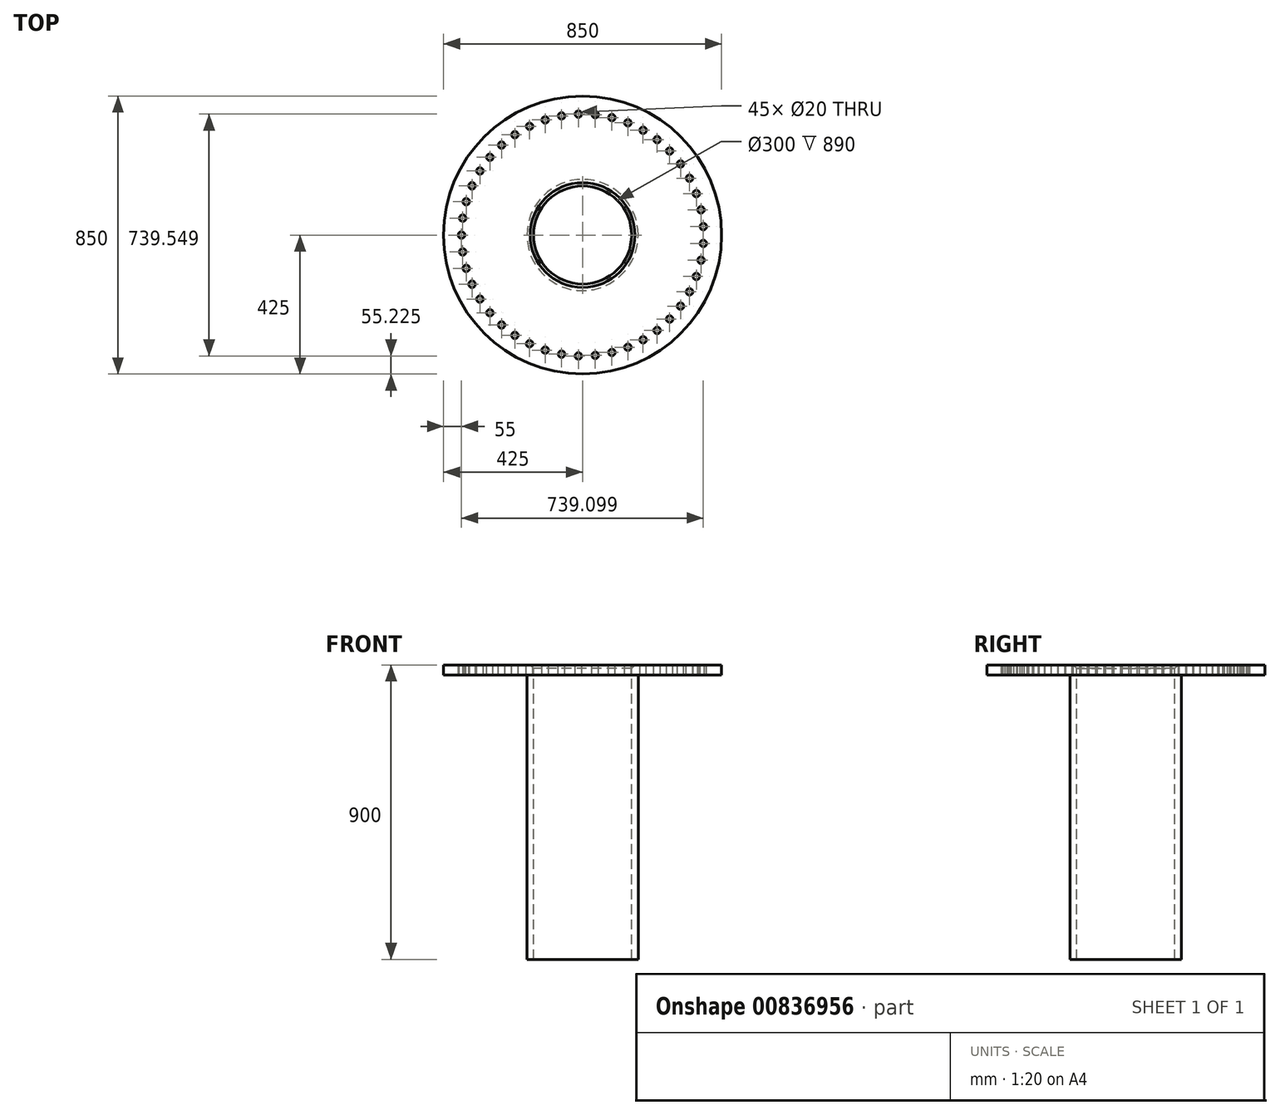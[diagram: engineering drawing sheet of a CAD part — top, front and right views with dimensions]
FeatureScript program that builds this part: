
annotation { "Feature Type Name" : "Feature", "Feature Type Description" : "" }
export const myFeature = defineFeature(function(context is Context, id is Id, definition is map)
    precondition{}
    {
        {
            var Q0;
            Q0=qCreatedBy(makeId("Top.planeOp"),FACE);
            var sketch = newSketch(context, id + "F0", { "sketchPlane" : qUnion([Q0])});
            skLineSegment(sketch, "E0.bottom", {"start": v(-1185, 450) * mm, "end": v(1185, 450) * mm});
            skLineSegment(sketch, "E0.top", {"start": v(-1185, -450) * mm, "end": v(1185, -450) * mm});
            skLineSegment(sketch, "E0.left", {"start": v(-1185, 450) * mm, "end": v(-1185, -450) * mm});
            skLineSegment(sketch, "E0.right", {"start": v(1185, 450) * mm, "end": v(1185, -450) * mm});
            skPoint(sketch, "E0.middle", {"position": v(0, 0) * mm});
            skLineSegment(sketch, "E1.bottom", {"start": v(-1185, 450) * mm, "end": v(-1141.5, 450) * mm});
            skLineSegment(sketch, "E1.top", {"start": v(-1185, -450) * mm, "end": v(-1141.5, -450) * mm});
            skLineSegment(sketch, "E1.right", {"start": v(-1141.49, 450) * mm, "end": v(-1141.49, -450) * mm});
            skLineSegment(sketch, "E2", {"start": v(1185, 0) * mm, "end": v(-1185, 0) * mm, "construction": true});
            skLineSegment(sketch, "E3", {"start": v(-92.5, -600) * mm, "end": v(-92.5, 600) * mm, "construction": true});
            skCircle(sketch, "E4", {"center": v(-92.5, 0) * mm, "radius": 600 * mm});
            skCircle(sketch, "E5", {"center": v(-92.5, 0) * mm, "radius": 550 * mm});
            skCircle(sketch, "E6", {"center": v(-92.5, 0) * mm, "radius": 425 * mm});
            skCircle(sketch, "E7", {"center": v(-92.5, 0) * mm, "radius": 525 * mm});
            skCircle(sketch, "E8", {"center": v(-617.5, 0) * mm, "radius": 10 * mm});
            skCircle(sketch, "E9.1.0", {"center": v(-612.4, -73.07) * mm, "radius": 10 * mm});
            skCircle(sketch, "E9.2.0", {"center": v(-597.16, -144.7) * mm, "radius": 10 * mm});
            skCircle(sketch, "E10.1.3.0", {"center": v(-572.11, -213.54) * mm, "radius": 10 * mm});
            skCircle(sketch, "E10.1.4.0", {"center": v(-537.73, -278.2) * mm, "radius": 10 * mm});
            skCircle(sketch, "E10.1.5.0", {"center": v(-494.67, -337.46) * mm, "radius": 10 * mm});
            skCircle(sketch, "E10.1.6.0", {"center": v(-443.8, -390.15) * mm, "radius": 10 * mm});
            skCircle(sketch, "E10.1.7.0", {"center": v(-386.08, -435.24) * mm, "radius": 10 * mm});
            skCircle(sketch, "E10.1.8.0", {"center": v(-322.64, -471.87) * mm, "radius": 10 * mm});
            skCircle(sketch, "E10.1.9.0", {"center": v(-254.73, -499.3) * mm, "radius": 10 * mm});
            skCircle(sketch, "E10.1.10.0", {"center": v(-183.67, -517.02) * mm, "radius": 10 * mm});
            skCircle(sketch, "E10.1.11.0", {"center": v(-110.82, -524.68) * mm, "radius": 10 * mm});
            skCircle(sketch, "E10.1.12.0", {"center": v(-37.62, -522.12) * mm, "radius": 10 * mm});
            skCircle(sketch, "E10.1.13.0", {"center": v(34.5, -509.4) * mm, "radius": 10 * mm});
            skCircle(sketch, "E10.1.14.0", {"center": v(104.17, -486.77) * mm, "radius": 10 * mm});
            skCircle(sketch, "E10.1.15.0", {"center": v(170, -454.66) * mm, "radius": 10 * mm});
            skCircle(sketch, "E10.1.16.0", {"center": v(230.72, -413.7) * mm, "radius": 10 * mm});
            skCircle(sketch, "E10.1.17.0", {"center": v(285.15, -364.7) * mm, "radius": 10 * mm});
            skCircle(sketch, "E10.1.18.0", {"center": v(332.23, -308.59) * mm, "radius": 10 * mm});
            skCircle(sketch, "E10.1.19.0", {"center": v(371.05, -246.47) * mm, "radius": 10 * mm});
            skCircle(sketch, "E10.1.20.0", {"center": v(400.84, -179.56) * mm, "radius": 10 * mm});
            skCircle(sketch, "E10.1.21.0", {"center": v(421.03, -109.15) * mm, "radius": 10 * mm});
            skCircle(sketch, "E10.1.22.0", {"center": v(431.22, -36.62) * mm, "radius": 10 * mm});
            skCircle(sketch, "E10.1.23.0", {"center": v(431.22, 36.62) * mm, "radius": 10 * mm});
            skCircle(sketch, "E10.1.24.0", {"center": v(421.03, 109.15) * mm, "radius": 10 * mm});
            skCircle(sketch, "E10.1.25.0", {"center": v(400.84, 179.56) * mm, "radius": 10 * mm});
            skCircle(sketch, "E10.1.26.0", {"center": v(371.05, 246.47) * mm, "radius": 10 * mm});
            skCircle(sketch, "E10.1.27.0", {"center": v(332.23, 308.59) * mm, "radius": 10 * mm});
            skCircle(sketch, "E10.1.28.0", {"center": v(285.15, 364.7) * mm, "radius": 10 * mm});
            skCircle(sketch, "E10.1.29.0", {"center": v(230.72, 413.7) * mm, "radius": 10 * mm});
            skCircle(sketch, "E10.1.30.0", {"center": v(170, 454.66) * mm, "radius": 10 * mm});
            skCircle(sketch, "E10.1.31.0", {"center": v(104.17, 486.77) * mm, "radius": 10 * mm});
            skCircle(sketch, "E10.1.32.0", {"center": v(34.5, 509.4) * mm, "radius": 10 * mm});
            skCircle(sketch, "E10.1.33.0", {"center": v(-37.62, 522.12) * mm, "radius": 10 * mm});
            skCircle(sketch, "E10.1.34.0", {"center": v(-110.82, 524.68) * mm, "radius": 10 * mm});
            skCircle(sketch, "E10.1.35.0", {"center": v(-183.67, 517.02) * mm, "radius": 10 * mm});
            skCircle(sketch, "E10.1.36.0", {"center": v(-254.73, 499.3) * mm, "radius": 10 * mm});
            skCircle(sketch, "E10.1.37.0", {"center": v(-322.64, 471.87) * mm, "radius": 10 * mm});
            skCircle(sketch, "E10.1.38.0", {"center": v(-386.08, 435.24) * mm, "radius": 10 * mm});
            skCircle(sketch, "E10.1.39.0", {"center": v(-443.8, 390.15) * mm, "radius": 10 * mm});
            skCircle(sketch, "E10.1.40.0", {"center": v(-494.67, 337.46) * mm, "radius": 10 * mm});
            skCircle(sketch, "E10.1.41.0", {"center": v(-537.73, 278.2) * mm, "radius": 10 * mm});
            skCircle(sketch, "E10.1.42.0", {"center": v(-572.11, 213.54) * mm, "radius": 10 * mm});
            skCircle(sketch, "E10.1.43.0", {"center": v(-597.16, 144.7) * mm, "radius": 10 * mm});
            skCircle(sketch, "E10.1.44.0", {"center": v(-612.4, 73.07) * mm, "radius": 10 * mm});
            skCircle(sketch, "E11", {"center": v(-92.5, 0) * mm, "radius": 370 * mm});
            skCircle(sketch, "E12", {"center": v(-462.5, 0) * mm, "radius": 10 * mm});
            skCircle(sketch, "E13.1.0", {"center": v(-458.9, -51.5) * mm, "radius": 10 * mm});
            skCircle(sketch, "E13.2.0", {"center": v(-448.17, -101.99) * mm, "radius": 10 * mm});
            skCircle(sketch, "E13.3.0", {"center": v(-430.51, -150.5) * mm, "radius": 10 * mm});
            skCircle(sketch, "E13.4.0", {"center": v(-406.28, -196.07) * mm, "radius": 10 * mm});
            skCircle(sketch, "E13.5.0", {"center": v(-375.94, -237.83) * mm, "radius": 10 * mm});
            skCircle(sketch, "E13.6.0", {"center": v(-340.08, -274.96) * mm, "radius": 10 * mm});
            skCircle(sketch, "E13.7.0", {"center": v(-299.4, -306.74) * mm, "radius": 10 * mm});
            skCircle(sketch, "E13.8.0", {"center": v(-254.7, -332.55) * mm, "radius": 10 * mm});
            skCircle(sketch, "E13.9.0", {"center": v(-206.84, -351.9) * mm, "radius": 10 * mm});
            skCircle(sketch, "E13.10.0", {"center": v(-156.75, -364.38) * mm, "radius": 10 * mm});
            skCircle(sketch, "E13.11.0", {"center": v(-105.41, -369.77) * mm, "radius": 10 * mm});
            skCircle(sketch, "E13.12.0", {"center": v(-53.82, -367.97) * mm, "radius": 10 * mm});
            skCircle(sketch, "E13.13.0", {"center": v(-2.99, -359) * mm, "radius": 10 * mm});
            skCircle(sketch, "E13.14.0", {"center": v(46.1, -343.06) * mm, "radius": 10 * mm});
            skCircle(sketch, "E13.15.0", {"center": v(92.5, -320.43) * mm, "radius": 10 * mm});
            skCircle(sketch, "E13.16.0", {"center": v(135.3, -291.56) * mm, "radius": 10 * mm});
            skCircle(sketch, "E13.17.0", {"center": v(173.66, -257.02) * mm, "radius": 10 * mm});
            skCircle(sketch, "E13.18.0", {"center": v(206.84, -217.48) * mm, "radius": 10 * mm});
            skCircle(sketch, "E13.19.0", {"center": v(234.2, -173.7) * mm, "radius": 10 * mm});
            skCircle(sketch, "E13.20.0", {"center": v(255.19, -126.55) * mm, "radius": 10 * mm});
            skCircle(sketch, "E13.21.0", {"center": v(269.41, -76.93) * mm, "radius": 10 * mm});
            skCircle(sketch, "E13.22.0", {"center": v(276.6, -25.8) * mm, "radius": 10 * mm});
            skCircle(sketch, "E13.23.0", {"center": v(276.6, 25.8) * mm, "radius": 10 * mm});
            skCircle(sketch, "E13.24.0", {"center": v(269.41, 76.93) * mm, "radius": 10 * mm});
            skCircle(sketch, "E13.25.0", {"center": v(255.19, 126.55) * mm, "radius": 10 * mm});
            skCircle(sketch, "E13.26.0", {"center": v(234.2, 173.7) * mm, "radius": 10 * mm});
            skCircle(sketch, "E13.27.0", {"center": v(206.84, 217.48) * mm, "radius": 10 * mm});
            skCircle(sketch, "E13.28.0", {"center": v(173.66, 257.02) * mm, "radius": 10 * mm});
            skCircle(sketch, "E13.29.0", {"center": v(135.3, 291.56) * mm, "radius": 10 * mm});
            skCircle(sketch, "E13.30.0", {"center": v(92.5, 320.43) * mm, "radius": 10 * mm});
            skCircle(sketch, "E13.31.0", {"center": v(46.1, 343.06) * mm, "radius": 10 * mm});
            skCircle(sketch, "E13.32.0", {"center": v(-2.99, 359) * mm, "radius": 10 * mm});
            skCircle(sketch, "E13.33.0", {"center": v(-53.82, 367.97) * mm, "radius": 10 * mm});
            skCircle(sketch, "E13.34.0", {"center": v(-105.41, 369.77) * mm, "radius": 10 * mm});
            skCircle(sketch, "E13.35.0", {"center": v(-156.75, 364.38) * mm, "radius": 10 * mm});
            skCircle(sketch, "E13.36.0", {"center": v(-206.84, 351.9) * mm, "radius": 10 * mm});
            skCircle(sketch, "E13.37.0", {"center": v(-254.7, 332.55) * mm, "radius": 10 * mm});
            skCircle(sketch, "E13.38.0", {"center": v(-299.4, 306.74) * mm, "radius": 10 * mm});
            skCircle(sketch, "E13.39.0", {"center": v(-340.08, 274.96) * mm, "radius": 10 * mm});
            skCircle(sketch, "E13.40.0", {"center": v(-375.94, 237.83) * mm, "radius": 10 * mm});
            skCircle(sketch, "E13.41.0", {"center": v(-406.28, 196.07) * mm, "radius": 10 * mm});
            skCircle(sketch, "E13.42.0", {"center": v(-430.51, 150.5) * mm, "radius": 10 * mm});
            skCircle(sketch, "E13.43.0", {"center": v(-448.17, 101.99) * mm, "radius": 10 * mm});
            skCircle(sketch, "E13.44.0", {"center": v(-458.9, 51.5) * mm, "radius": 10 * mm});
            skLineSegment(sketch, "E14.bottom", {"start": v(-925, 450) * mm, "end": v(-735, 450) * mm});
            skLineSegment(sketch, "E14.top", {"start": v(-925, 315) * mm, "end": v(-735, 315) * mm});
            skLineSegment(sketch, "E14.left", {"start": v(-925, 450) * mm, "end": v(-925, 315) * mm});
            skLineSegment(sketch, "E14.right", {"start": v(-735, 450) * mm, "end": v(-735, 315) * mm});
            skLineSegment(sketch, "E15.bottom", {"start": v(-913, 327) * mm, "end": v(-747, 327) * mm});
            skLineSegment(sketch, "E15.top", {"start": v(-913, 438) * mm, "end": v(-747, 438) * mm});
            skLineSegment(sketch, "E15.left", {"start": v(-913, 327) * mm, "end": v(-913, 438) * mm});
            skLineSegment(sketch, "E15.right", {"start": v(-747, 327) * mm, "end": v(-747, 438) * mm});
            skPoint(sketch, "E15.middle", {"position": v(-830, 382.5) * mm});
            skLineSegment(sketch, "E16.MirrorCS", {"start": v(-735, -450) * mm, "end": v(-735, -315) * mm});
            skLineSegment(sketch, "E17.MirrorCS", {"start": v(-925, -315) * mm, "end": v(-735, -315) * mm});
            skLineSegment(sketch, "E18.MirrorCS", {"start": v(-913, -438) * mm, "end": v(-747, -438) * mm});
            skLineSegment(sketch, "E19.MirrorCS", {"start": v(-925, -450) * mm, "end": v(-925, -315) * mm});
            skLineSegment(sketch, "E20.MirrorCS", {"start": v(-747, -327) * mm, "end": v(-747, -438) * mm});
            skPoint(sketch, "E21.MirrorP", {"position": v(-830, -382.5) * mm});
            skLineSegment(sketch, "E22.MirrorCS", {"start": v(-913, -327) * mm, "end": v(-913, -438) * mm});
            skLineSegment(sketch, "E23.MirrorCS", {"start": v(-913, -327) * mm, "end": v(-747, -327) * mm});
            skLineSegment(sketch, "E24.MirrorCS", {"start": v(-925, -450) * mm, "end": v(-735, -450) * mm});
            skArc(sketch, "E25", {"start": v(-301.83, -562.3) * mm, "mid": v(-739.86, -478.19) * mm, "end": v(-1185, -450) * mm});
            skArc(sketch, "E26.MirrorCS", {"start": v(-301.83, 562.3) * mm, "mid": v(-739.86, 478.19) * mm, "end": v(-1185, 450) * mm});
            skCircle(sketch, "E27", {"center": v(-92.5, 0) * mm, "radius": 325 * mm});
            skCircle(sketch, "E28", {"center": v(-92.5, 0) * mm, "radius": 150 * mm});
            skCircle(sketch, "E29", {"center": v(-92.5, 0) * mm, "radius": 170 * mm});
            skSolve(sketch);
        }
        {
            var Q0;
            {var subQ130=sQuery(id+"F0.wireOp",EDGE,"E6");var subQ131=makeQuery(id+"F0.imprint","INTERSECT",VERTEX,{"derivedFrom":[sQuery(id+"F0.wireOp",EDGE,"E0.bottom"),subQ130]});Q0=makeQuery(id+"F0.imprint","IMPRINT",FACE,{"disambiguationData":[TD([[makeQuery(id+"F0.imprint","IMPRINT",EDGE,{"disambiguationData":[TD([[subQ131,-1.0]])],"derivedFrom":subQ130}),1.0]])]});}
            var Q1;
            Q1=makeQuery(id+"F0.imprint","IMPRINT",FACE,{"disambiguationData":[TD([[makeQuery(id+"F0.imprint","IMPRINT",EDGE,{"derivedFrom":sQuery(id+"F0.wireOp",EDGE,"E27")}),-1.0]])]});
            var Q2;
            Q2=makeQuery(id+"F0.imprint","IMPRINT",FACE,{"disambiguationData":[TD([[makeQuery(id+"F0.imprint","IMPRINT",EDGE,{"derivedFrom":sQuery(id+"F0.wireOp",EDGE,"E27")}),1.0]])]});
            extrude(context, id + "F1", {"entities" : qUnion([Q0, Q1, Q2]), "oppositeDirection" : true, "depth" : 30 * mm, "offsetDistance" : 25 * mm});
        }
        {
            var Q0;
            Q0=makeQuery(id+"F0.imprint","IMPRINT",FACE,{"disambiguationData":[TD([[makeQuery(id+"F0.imprint","IMPRINT",EDGE,{"derivedFrom":sQuery(id+"F0.wireOp",EDGE,"E28")}),-1.0]])]});
            extrude(context, id + "F2", {"entities" : qUnion([Q0]), "operationType" : NewBodyOperationType.ADD, "oppositeDirection" : true, "depth" : 900 * mm, "offsetDistance" : 25 * mm});
        }
        {
            var Q0;
            Q0=makeQuery(id+"F2.opExtrude","CAP_EDGE",EDGE,{"disambiguationData":[OSD([sQuery(id+"F0.wireOp",EDGE,"E28")])],"isStart":true});
            chamfer(context, id + "F3", {"entities" : qUnion([Q0]), "width" : 10 * mm, "tangentPropagation" : true});
        }
    });
